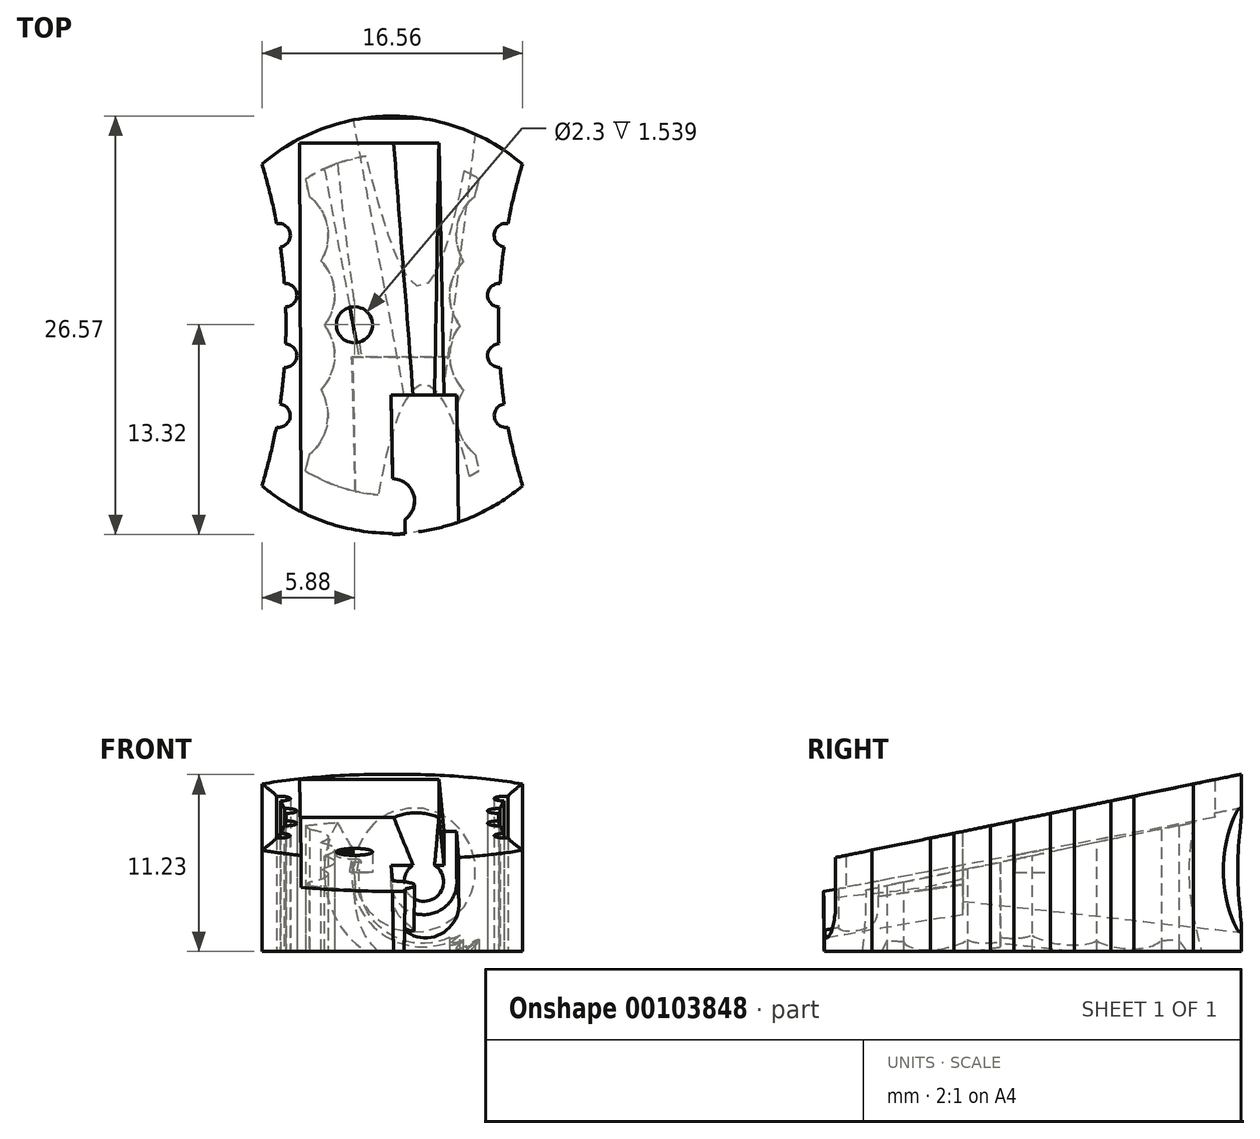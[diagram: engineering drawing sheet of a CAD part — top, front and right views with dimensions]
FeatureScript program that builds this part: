
annotation { "Feature Type Name" : "Feature", "Feature Type Description" : "" }
export const myFeature = defineFeature(function(context is Context, id is Id, definition is map)
    precondition{}
    {
        {
            var Q0;
            Q0=qCreatedBy(makeId("Top.planeOp"),FACE);
            var sketch = newSketch(context, id + "F0", { "sketchPlane" : qUnion([Q0])});
            skArc(sketch, "E0", {"start": v(-8.02, 9.64) * mm, "mid": v(-8.05, 9.61) * mm, "end": v(-8.09, 9.59) * mm, "construction": true});
            skArc(sketch, "E1", {"start": v(0, 13.25) * mm, "mid": v(-4.4, 12.46) * mm, "end": v(-8.27, 10.2) * mm});
            skArc(sketch, "E2", {"start": v(-8.28, -10.23) * mm, "mid": v(-6.76, 0.87) * mm, "end": v(-8.83, 11.88) * mm});
            skLineSegment(sketch, "E3", {"start": v(0, 27.52) * mm, "end": v(0, -29.67) * mm});
            skLineSegment(sketch, "E4", {"start": v(0, 13.25) * mm, "end": v(1.48, 13.25) * mm});
            skLineSegment(sketch, "E5", {"start": v(-7.8, 10.6) * mm, "end": v(-9.31, 9.42) * mm});
            skLineSegment(sketch, "E6", {"start": v(-9.2, 12.93) * mm, "end": v(-8.83, 11.88) * mm});
            skArc(sketch, "E7.trimOffspring", {"start": v(-8.28, -10.23) * mm, "mid": v(-4.4, -12.47) * mm, "end": v(0, -13.25) * mm});
            skLineSegment(sketch, "E8", {"start": v(0, -13.25) * mm, "end": v(1.48, -13.25) * mm});
            skCircle(sketch, "E9", {"center": v(-7.22, 5.69) * mm, "radius": 0.75 * mm});
            skCircle(sketch, "E10.1.0", {"center": v(-6.8, 1.88) * mm, "radius": 0.75 * mm});
            skCircle(sketch, "E10.2.0", {"center": v(-6.8, -1.96) * mm, "radius": 0.75 * mm});
            skCircle(sketch, "E10.3.0", {"center": v(-7.23, -5.77) * mm, "radius": 0.75 * mm});
            skLineSegment(sketch, "E10.anchor1", {"start": v(-41.75, 0) * mm, "end": v(-7.22, 5.69) * mm, "construction": true});
            skLineSegment(sketch, "E10.anchor2", {"start": v(-41.75, 0) * mm, "end": v(-7.23, -5.77) * mm, "construction": true});
            skSolve(sketch);
        }
        {
            var Q0;
            {var subQ3=sQuery(id+"F0.wireOp",EDGE,"E7.trimOffspring");Q0=makeQuery(id+"F0.imprint","IMPRINT",FACE,{"disambiguationData":[TD([[makeQuery(id+"F0.imprint","IMPRINT",EDGE,{"derivedFrom":subQ3}),1.0]])]});}
            extrude(context, id + "F1", {"entities" : qUnion([Q0]), "depth" : 11.23 * mm});
        }
        {
            var Q0;
            Q0=makeQuery(id+"F1.opExtrude","SWEPT_BODY",BODY,{"disambiguationData":[OSD([sQuery(id+"F0.wireOp",EDGE,"E1"),sQuery(id+"F0.wireOp",EDGE,"E2"),sQuery(id+"F0.wireOp",EDGE,"E3"),sQuery(id+"F0.wireOp",EDGE,"E7.trimOffspring")])]});
            var Q1;
            Q1=qCreatedBy(makeId("Right.planeOp"),FACE);
            mirror(context, id + "F2", {"operationType" : NewBodyOperationType.ADD, "entities" : qUnion([Q0]), "mirrorPlane" : qUnion([Q1])});
        }
        {
            var Q0;
            Q0=qCreatedBy(makeId("Right.planeOp"),FACE);
            var sketch = newSketch(context, id + "F3", { "sketchPlane" : qUnion([Q0])});
            skLineSegment(sketch, "E11", {"start": v(10.2, 10.63) * mm, "end": v(-10.23, 6.43) * mm});
            skLineSegment(sketch, "E12", {"start": v(15.76, 11.77) * mm, "end": v(-16.6, 5.12) * mm});
            skPoint(sketch, "E13.end.orphan", {"position": v(10.2, 0) * mm});
            skPoint(sketch, "E14.end.orphan", {"position": v(-10.23, 0) * mm});
            skLineSegment(sketch, "E15", {"start": v(15.76, 11.77) * mm, "end": v(15.76, 16.34) * mm});
            skLineSegment(sketch, "E16", {"start": v(15.76, 16.34) * mm, "end": v(-16.6, 16.34) * mm});
            skLineSegment(sketch, "E17", {"start": v(-16.6, 16.34) * mm, "end": v(-16.6, 5.12) * mm});
            skLineSegment(sketch, "E18", {"start": v(15.76, 11.77) * mm, "end": v(15.76, -3.68) * mm});
            skLineSegment(sketch, "E19", {"start": v(15.76, -3.68) * mm, "end": v(-16.6, -3.68) * mm});
            skLineSegment(sketch, "E20", {"start": v(-16.6, -3.68) * mm, "end": v(-16.6, 5.12) * mm});
            skSolve(sketch);
        }
        {
            var Q0;
            {var subQ0=sQuery(id+"F3.wireOp",EDGE,"E18");Q0=makeQuery(id+"F3.imprint","IMPRINT",FACE,{"disambiguationData":[TD([[makeQuery(id+"F3.imprint","IMPRINT",EDGE,{"derivedFrom":subQ0}),-1.0]])]});}
            extrude(context, id + "F4", {"entities" : qUnion([Q0]), "operationType" : NewBodyOperationType.INTERSECT, "endBound" : BoundingType.SYMMETRIC, "depth" : 21.66 * mm});
        }
        {
            var Q0;
            Q0=qCreatedBy(makeId("Right.planeOp"),FACE);
            cPlane(context, id + "F5", {"entities" : qUnion([Q0]), "cplaneType" : CPlaneType.OFFSET, "offset" : 3 * mm, "width" : 150 * mm, "height" : 150 * mm});
        }
        {
            var Q0;
            Q0=qCreatedBy(makeId("Front.planeOp"),FACE);
            cPlane(context, id + "F6", {"entities" : qUnion([Q0]), "cplaneType" : CPlaneType.OFFSET, "offset" : 13.25 * mm, "oppositeDirection" : true, "width" : 150 * mm, "height" : 150 * mm});
        }
        {
            var Q0;
            Q0=qCreatedBy(id+"F6.planeOp",FACE);
            var sketch = newSketch(context, id + "F7", { "sketchPlane" : qUnion([Q0])});
            skCircle(sketch, "E21", {"center": v(1.48, 5.16) * mm, "radius": 3.96 * mm});
            skLineSegment(sketch, "E22", {"start": v(5.44, 8.88) * mm, "end": v(5.44, 1.93) * mm});
            skLineSegment(sketch, "E23", {"start": v(6.15, 1.2) * mm, "end": v(-1.11, 1.2) * mm});
            skLineSegment(sketch, "E24", {"start": v(4.75, 9.13) * mm, "end": v(-1.65, 9.13) * mm});
            skSolve(sketch);
        }
        {
            var Q0;
            Q0=qCreatedBy(id+"F5.planeOp",FACE);
            var sketch = newSketch(context, id + "F8", { "sketchPlane" : qUnion([Q0])});
            skLineSegment(sketch, "E25", {"start": v(13.25, 8.83) * mm, "end": v(-16.57, 2.7) * mm});
            skLineSegment(sketch, "E26", {"start": v(13.25, 1.5) * mm, "end": v(-17.13, 5.21) * mm});
            skSolve(sketch);
        }
        {
            var Q0;
            Q0=qCreatedBy(id+"F6.planeOp",FACE);
            cPlane(context, id + "F9", {"entities" : qUnion([Q0]), "cplaneType" : CPlaneType.OFFSET, "offset" : 17.7 * mm, "width" : 150 * mm, "height" : 150 * mm});
        }
        {
            var Q0;
            Q0=qCreatedBy(id+"F9.planeOp",FACE);
            var sketch = newSketch(context, id + "F10", { "sketchPlane" : qUnion([Q0])});
            skCircle(sketch, "E27", {"center": v(2, 4.43) * mm, "radius": 1.25 * mm});
            skSolve(sketch);
        }
        {
            var Q1;
            Q1=makeQuery(id+"F7.imprint","IMPRINT",FACE,{"disambiguationData":[TD([[makeQuery(id+"F7.imprint","IMPRINT",EDGE,{"derivedFrom":sQuery(id+"F7.wireOp",EDGE,"E21")}),1.0]])]});
            var Q2;
            Q2=qSketchRegion(id+"F10",true);
            loft(context, id + "F11", {"operationType" : NewBodyOperationType.REMOVE, "sheetProfilesArray" : [{ "sheetProfileEntities" : qUnion([Q1]) }, { "sheetProfileEntities" : qUnion([Q2]) }]});
        }
        {
            var Q0;
            Q0=qCreatedBy(id+"F6.planeOp",FACE);
            cPlane(context, id + "F12", {"entities" : qUnion([Q0]), "cplaneType" : CPlaneType.OFFSET, "offset" : 26.6 * mm, "width" : 150 * mm, "height" : 150 * mm});
        }
        {
            var Q0;
            Q0=qCreatedBy(id+"F9.planeOp",FACE);
            var sketch = newSketch(context, id + "F13", { "sketchPlane" : qUnion([Q0])});
            skCircle(sketch, "E28", {"center": v(2, 4.43) * mm, "radius": 2.1 * mm});
            skSolve(sketch);
        }
        {
            var Q0;
            Q0=qCreatedBy(id+"F12.planeOp",FACE);
            var sketch = newSketch(context, id + "F14", { "sketchPlane" : qUnion([Q0])});
            skCircle(sketch, "E29", {"center": v(2.18, 2.9) * mm, "radius": 2.1 * mm});
            skSolve(sketch);
        }
        {
            var Q1;
            Q1=qSketchRegion(id+"F13",true);
            var Q2;
            Q2=qSketchRegion(id+"F14",true);
            loft(context, id + "F15", {"operationType" : NewBodyOperationType.REMOVE, "sheetProfilesArray" : [{ "sheetProfileEntities" : qUnion([Q1]) }, { "sheetProfileEntities" : qUnion([Q2]) }]});
        }
        {
            var Q0;
            {var subQ0=makeQuery(id+"F1.opExtrude","CAP_FACE",FACE,{"disambiguationData":[OSD([sQuery(id+"F0.wireOp",EDGE,"E1"),sQuery(id+"F0.wireOp",EDGE,"E2"),sQuery(id+"F0.wireOp",EDGE,"E3"),sQuery(id+"F0.wireOp",EDGE,"E7.trimOffspring")])],"isStart":true});Q0=makeQuery(id+"F2.boolean.opBoolean","MERGE",FACE,{"derivedFrom":[subQ0,makeQuery(id+"F2.opPattern","COPY",FACE,{"derivedFrom":subQ0,"instanceName":"1"})]});}
            shell(context, id + "F16", {"entities" : qUnion([Q0]), "thickness" : 2.4 * mm});
        }
        {
            var Q0;
            Q0=qCreatedBy(id+"F12.planeOp",FACE);
            var sketch = newSketch(context, id + "F17", { "sketchPlane" : qUnion([Q0])});
            skLineSegment(sketch, "E30", {"start": v(-5.78, 3.79) * mm, "end": v(3.46, 3.79) * mm});
            skLineSegment(sketch, "E31", {"start": v(3.46, 3.79) * mm, "end": v(3.46, 5.79) * mm});
            skLineSegment(sketch, "E32", {"start": v(3.46, 5.79) * mm, "end": v(-5.78, 5.79) * mm});
            skLineSegment(sketch, "E33", {"start": v(-5.78, 3.79) * mm, "end": v(-5.78, 5.79) * mm});
            skSolve(sketch);
        }
        {
            var Q0;
            Q0=qCreatedBy(id+"F6.planeOp",FACE);
            cPlane(context, id + "F18", {"entities" : qUnion([Q0]), "cplaneType" : CPlaneType.OFFSET, "offset" : 1.7 * mm, "width" : 150 * mm, "height" : 150 * mm});
        }
        {
            var Q0;
            Q0=qCreatedBy(id+"F18.planeOp",FACE);
            var sketch = newSketch(context, id + "F19", { "sketchPlane" : qUnion([Q0])});
            skLineSegment(sketch, "E34", {"start": v(2.97, 10.9) * mm, "end": v(-5.87, 10.9) * mm});
            skLineSegment(sketch, "E35", {"start": v(-5.87, 10.9) * mm, "end": v(-5.87, 8.5) * mm});
            skLineSegment(sketch, "E36", {"start": v(-5.87, 8.5) * mm, "end": v(2.97, 8.5) * mm});
            skLineSegment(sketch, "E37", {"start": v(2.97, 8.5) * mm, "end": v(2.97, 10.9) * mm});
            skSolve(sketch);
        }
        {
            var Q0;
            Q0=qCreatedBy(id+"F9.planeOp",FACE);
            var sketch = newSketch(context, id + "F20", { "sketchPlane" : qUnion([Q0])});
            skLineSegment(sketch, "E38.bottom", {"start": v(-0.08, 4.24) * mm, "end": v(4.1, 4.24) * mm});
            skLineSegment(sketch, "E38.top", {"start": v(-0.08, 10.02) * mm, "end": v(4.1, 10.02) * mm});
            skLineSegment(sketch, "E38.left", {"start": v(-0.08, 10.02) * mm, "end": v(-0.08, 4.24) * mm});
            skLineSegment(sketch, "E38.right", {"start": v(4.1, 10.02) * mm, "end": v(4.1, 4.24) * mm});
            skSolve(sketch);
        }
        {
            var Q0;
            Q0=qCreatedBy(id+"F12.planeOp",FACE);
            var sketch = newSketch(context, id + "F21", { "sketchPlane" : qUnion([Q0])});
            skLineSegment(sketch, "E39.bottom", {"start": v(0.08, 9.94) * mm, "end": v(4.23, 9.94) * mm});
            skLineSegment(sketch, "E39.top", {"start": v(0.08, 3) * mm, "end": v(4.23, 3) * mm});
            skLineSegment(sketch, "E39.left", {"start": v(0.08, 3) * mm, "end": v(0.08, 9.94) * mm});
            skLineSegment(sketch, "E39.right", {"start": v(4.23, 3) * mm, "end": v(4.23, 9.94) * mm});
            skSolve(sketch);
        }
        {
            var Q1;
            Q1=qSketchRegion(id+"F21",true);
            var Q2;
            Q2=qSketchRegion(id+"F20",true);
            loft(context, id + "F22", {"operationType" : NewBodyOperationType.REMOVE, "sheetProfilesArray" : [{ "sheetProfileEntities" : qUnion([Q1]) }, { "sheetProfileEntities" : qUnion([Q2]) }]});
        }
        {
            var Q0;
            Q0=qCreatedBy(makeId("Top.planeOp"),FACE);
            var sketch = newSketch(context, id + "F23", { "sketchPlane" : qUnion([Q0])});
            skArc(sketch, "E40", {"start": v(0.76, -12.33) * mm, "mid": v(1.3, -10.81) * mm, "end": v(0, -9.85) * mm});
            skLineSegment(sketch, "E41.right", {"start": v(0.76, -12.33) * mm, "end": v(0.76, -13.23) * mm});
            skArc(sketch, "E42", {"start": v(0.08, -13.25) * mm, "mid": v(0.42, -13.24) * mm, "end": v(0.76, -13.23) * mm});
            skLineSegment(sketch, "E43", {"start": v(0.08, -13.25) * mm, "end": v(0, -9.85) * mm});
            skSolve(sketch);
        }
        {
            var Q0;
            Q0=qSketchRegion(id+"F23",true);
            extrude(context, id + "F24", {"entities" : qUnion([Q0]), "operationType" : NewBodyOperationType.ADD, "depth" : 4.8 * mm, "hasDraft" : true, "draftAngle" : 1 * degree});
        }
        {
            var Q1;
            Q1=qSketchRegion(id+"F19",true);
            var Q2;
            Q2=qSketchRegion(id+"F17",true);
            loft(context, id + "F25", {"operationType" : NewBodyOperationType.REMOVE, "sheetProfilesArray" : [{ "sheetProfileEntities" : qUnion([Q1]) }, { "sheetProfileEntities" : qUnion([Q2]) }]});
        }
        {
            var Q0;
            Q0=qCreatedBy(makeId("Top.planeOp"),FACE);
            var sketch = newSketch(context, id + "F26", { "sketchPlane" : qUnion([Q0])});
            skCircle(sketch, "E44", {"center": v(-2.4, 0) * mm, "radius": 1.15 * mm});
            skSolve(sketch);
        }
        {
            var Q0;
            Q0=qSketchRegion(id+"F26",true);
            var Q1;
            Q1=makeQuery(id+"F25.boolean.opBoolean","COPY",FACE,{"disambiguationData":[OD(1.0)],"derivedFrom":makeQuery(id+"F25.opLoft","SWEPT_FACE",FACE,{"disambiguationData":[OSD([sQuery(id+"F17.wireOp",EDGE,"E30"),sQuery(id+"F17.wireOp",EDGE,"E31"),sQuery(id+"F17.wireOp",EDGE,"E33"),sQuery(id+"F19.wireOp",EDGE,"E35"),sQuery(id+"F19.wireOp",EDGE,"E36"),sQuery(id+"F19.wireOp",EDGE,"E37")])]})});
            extrude(context, id + "F27", {"entities" : qUnion([Q0, Q1]), "operationType" : NewBodyOperationType.REMOVE, "depth" : 22 * mm, "hasSecondDirection" : true, "secondDirectionOppositeDirection" : false, "secondDirectionDepth" : 5 * mm});
        }
    });
